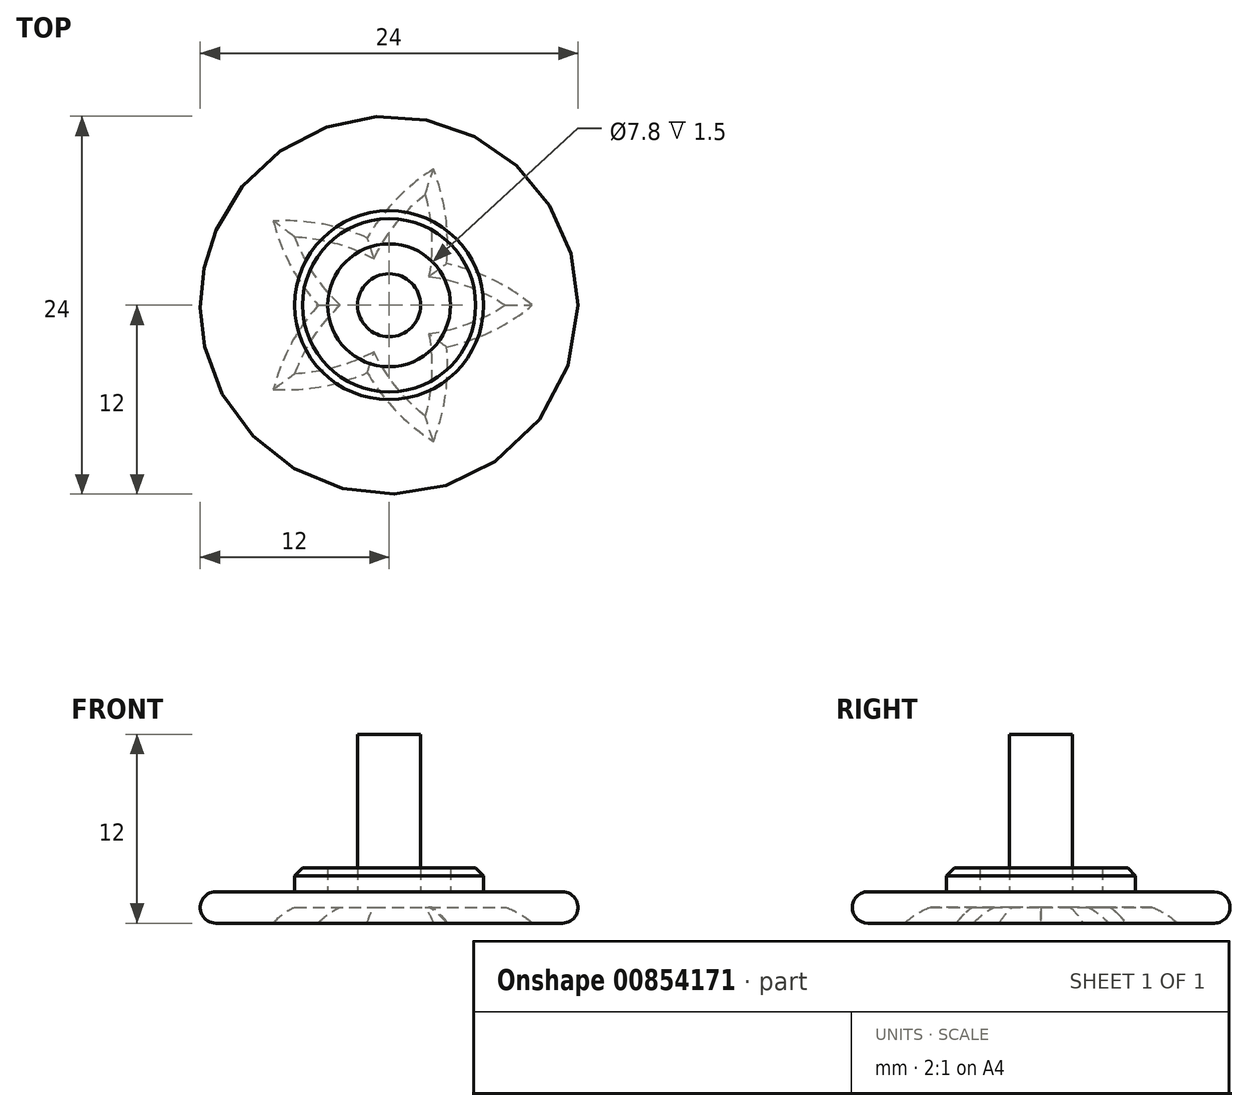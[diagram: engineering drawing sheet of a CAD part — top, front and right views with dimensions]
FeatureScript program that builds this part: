
annotation { "Feature Type Name" : "Feature", "Feature Type Description" : "" }
export const myFeature = defineFeature(function(context is Context, id is Id, definition is map)
    precondition{}
    {
        {
            var Q0;
            Q0=qCreatedBy(makeId("Top.planeOp"),FACE);
            var sketch = newSketch(context, id + "F0", { "sketchPlane" : qUnion([Q0])});
            skCircle(sketch, "E0", {"center": v(0, 0) * mm, "radius": 3.9 * mm});
            skCircle(sketch, "E1", {"center": v(0, 0) * mm, "radius": 2 * mm});
            skCircle(sketch, "E2", {"center": v(0, 0) * mm, "radius": 12 * mm});
            skCircle(sketch, "E3", {"center": v(0, 0) * mm, "radius": 6 * mm});
            skCircle(sketch, "E4.cCircle", {"center": v(0, 0) * mm, "radius": 2.5 * mm, "construction": true});
            skLineSegment(sketch, "E4.0", {"start": v(-2.5, -1.82) * mm, "end": v(-2.5, 1.82) * mm});
            skLineSegment(sketch, "E4.1", {"start": v(-2.5, 1.82) * mm, "end": v(0.95, 2.94) * mm});
            skLineSegment(sketch, "E4.2", {"start": v(0.95, 2.94) * mm, "end": v(3.1, 0) * mm});
            skLineSegment(sketch, "E4.3", {"start": v(3.1, 0) * mm, "end": v(0.95, -2.94) * mm});
            skLineSegment(sketch, "E4.4", {"start": v(0.95, -2.94) * mm, "end": v(-2.5, -1.82) * mm});
            skPoint(sketch, "E4.0.midPoint", {"position": v(-2.5, 0) * mm});
            skLineSegment(sketch, "E5", {"start": v(-2.5, 0) * mm, "end": v(-4.5, 0) * mm});
            skLineSegment(sketch, "E6", {"start": v(-0.77, -2.38) * mm, "end": v(-1.4, -4.28) * mm});
            skLineSegment(sketch, "E7", {"start": v(2.02, -1.47) * mm, "end": v(3.64, -2.65) * mm});
            skLineSegment(sketch, "E8", {"start": v(2.02, 1.47) * mm, "end": v(3.64, 2.65) * mm});
            skLineSegment(sketch, "E9", {"start": v(-0.77, 2.38) * mm, "end": v(-1.4, 4.28) * mm});
            skLineSegment(sketch, "E10", {"start": v(3.1, 0) * mm, "end": v(9.1, 0) * mm});
            skLineSegment(sketch, "E11", {"start": v(0.95, -2.94) * mm, "end": v(2.8, -8.65) * mm});
            skLineSegment(sketch, "E12", {"start": v(-2.5, -1.82) * mm, "end": v(-7.35, -5.34) * mm});
            skLineSegment(sketch, "E13", {"start": v(-2.5, 1.82) * mm, "end": v(-7.35, 5.34) * mm});
            skLineSegment(sketch, "E14", {"start": v(0.95, 2.94) * mm, "end": v(2.8, 8.65) * mm});
            skArc(sketch, "E15", {"start": v(0.95, 2.94) * mm, "mid": v(-3, 4.86) * mm, "end": v(-7.35, 5.34) * mm});
            skArc(sketch, "E16", {"start": v(2.8, 8.65) * mm, "mid": v(-0.44, 5.7) * mm, "end": v(-2.5, 1.82) * mm});
            skArc(sketch, "E17", {"start": v(3.1, 0) * mm, "mid": v(3.7, 4.35) * mm, "end": v(2.8, 8.65) * mm});
            skArc(sketch, "E18", {"start": v(9.1, 0) * mm, "mid": v(5.28, 2.17) * mm, "end": v(0.95, 2.94) * mm});
            skArc(sketch, "E19", {"start": v(0.95, -2.94) * mm, "mid": v(5.28, -2.17) * mm, "end": v(9.1, 0) * mm});
            skArc(sketch, "E20", {"start": v(2.8, -8.65) * mm, "mid": v(3.7, -4.35) * mm, "end": v(3.1, 0) * mm});
            skArc(sketch, "E21", {"start": v(-2.5, -1.82) * mm, "mid": v(-0.44, -5.7) * mm, "end": v(2.8, -8.65) * mm});
            skArc(sketch, "E22", {"start": v(-7.35, -5.34) * mm, "mid": v(-3, -4.86) * mm, "end": v(0.95, -2.94) * mm});
            skArc(sketch, "E23", {"start": v(-2.5, 1.82) * mm, "mid": v(-5.55, -1.34) * mm, "end": v(-7.35, -5.34) * mm});
            skArc(sketch, "E24", {"start": v(-7.35, 5.34) * mm, "mid": v(-5.55, 1.34) * mm, "end": v(-2.5, -1.82) * mm});
            skSolve(sketch);
        }
        {
            var Q0;
            Q0=makeQuery(id+"F0.imprint","IMPRINT",FACE,{"disambiguationData":[TD([[makeQuery(id+"F0.imprint","IMPRINT",EDGE,{"derivedFrom":sQuery(id+"F0.wireOp",EDGE,"E2")}),1.0]])]});
            extrude(context, id + "F1", {"entities" : qUnion([Q0]), "depth" : 2 * mm, "offsetDistance" : 25 * mm});
        }
        {
            var Q0;
            {var subQ0=sQuery(id+"F0.wireOp",EDGE,"E15");var subQ1=sQuery(id+"F0.wireOp",EDGE,"E3");var subQ2=makeQuery(id+"F0.imprint","INTERSECT",VERTEX,{"derivedFrom":[subQ1,subQ0]});Q0=makeQuery(id+"F0.imprint","IMPRINT",FACE,{"disambiguationData":[TD([[makeQuery(id+"F0.imprint","IMPRINT",EDGE,{"disambiguationData":[TD([[subQ2,-1.0]])],"derivedFrom":subQ1}),-1.0]])]});}
            var Q1;
            {var subQ0=sQuery(id+"F0.wireOp",EDGE,"E13");var subQ1=sQuery(id+"F0.wireOp",EDGE,"E3");var subQ2=makeQuery(id+"F0.imprint","INTERSECT",VERTEX,{"derivedFrom":[subQ1,subQ0]});Q1=makeQuery(id+"F0.imprint","IMPRINT",FACE,{"disambiguationData":[TD([[makeQuery(id+"F0.imprint","IMPRINT",EDGE,{"disambiguationData":[TD([[subQ2,-1.0]])],"derivedFrom":subQ1}),-1.0]])]});}
            var Q2;
            {var subQ3=sQuery(id+"F0.wireOp",EDGE,"E0");var subQ5=sQuery(id+"F0.wireOp",EDGE,"E13");var subQ9=makeQuery(id+"F0.imprint","INTERSECT",VERTEX,{"derivedFrom":[subQ3,subQ5]});Q2=makeQuery(id+"F0.imprint","IMPRINT",FACE,{"disambiguationData":[TD([[makeQuery(id+"F0.imprint","IMPRINT",EDGE,{"disambiguationData":[TD([[subQ9,-1.0]])],"derivedFrom":subQ3}),-1.0]])]});}
            var Q3;
            {var subQ0=sQuery(id+"F0.wireOp",EDGE,"E16");var subQ6=sQuery(id+"F0.wireOp",EDGE,"E0");var subQ9=makeQuery(id+"F0.imprint","INTERSECT",VERTEX,{"derivedFrom":[subQ6,subQ0]});Q3=makeQuery(id+"F0.imprint","IMPRINT",FACE,{"disambiguationData":[TD([[makeQuery(id+"F0.imprint","IMPRINT",EDGE,{"disambiguationData":[TD([[subQ9,-1.0]])],"derivedFrom":subQ6}),-1.0]])]});}
            var Q4;
            {var subQ3=sQuery(id+"F0.wireOp",EDGE,"E0");var subQ5=sQuery(id+"F0.wireOp",EDGE,"E14");var subQ6=makeQuery(id+"F0.imprint","INTERSECT",VERTEX,{"derivedFrom":[subQ3,subQ5]});Q4=makeQuery(id+"F0.imprint","IMPRINT",FACE,{"disambiguationData":[TD([[makeQuery(id+"F0.imprint","IMPRINT",EDGE,{"disambiguationData":[TD([[subQ6,-1.0]])],"derivedFrom":subQ3}),-1.0]])]});}
            var Q5;
            {var subQ0=sQuery(id+"F0.wireOp",EDGE,"E14");var subQ1=sQuery(id+"F0.wireOp",EDGE,"E3");var subQ2=makeQuery(id+"F0.imprint","INTERSECT",VERTEX,{"derivedFrom":[subQ1,subQ0]});Q5=makeQuery(id+"F0.imprint","IMPRINT",FACE,{"disambiguationData":[TD([[makeQuery(id+"F0.imprint","IMPRINT",EDGE,{"disambiguationData":[TD([[subQ2,-1.0]])],"derivedFrom":subQ1}),-1.0]])]});}
            var Q6;
            {var subQ0=sQuery(id+"F0.wireOp",EDGE,"E17");var subQ1=sQuery(id+"F0.wireOp",EDGE,"E3");var subQ2=makeQuery(id+"F0.imprint","INTERSECT",VERTEX,{"derivedFrom":[subQ1,subQ0]});Q6=makeQuery(id+"F0.imprint","IMPRINT",FACE,{"disambiguationData":[TD([[makeQuery(id+"F0.imprint","IMPRINT",EDGE,{"disambiguationData":[TD([[subQ2,-1.0]])],"derivedFrom":subQ1}),-1.0]])]});}
            var Q7;
            {var subQ0=sQuery(id+"F0.wireOp",EDGE,"E18");var subQ6=sQuery(id+"F0.wireOp",EDGE,"E0");var subQ9=makeQuery(id+"F0.imprint","INTERSECT",VERTEX,{"derivedFrom":[subQ6,subQ0]});Q7=makeQuery(id+"F0.imprint","IMPRINT",FACE,{"disambiguationData":[TD([[makeQuery(id+"F0.imprint","IMPRINT",EDGE,{"disambiguationData":[TD([[subQ9,-1.0]])],"derivedFrom":subQ6}),-1.0]])]});}
            var Q8;
            {var subQ0=sQuery(id+"F0.wireOp",EDGE,"E15");var subQ1=sQuery(id+"F0.wireOp",EDGE,"E0");var subQ2=makeQuery(id+"F0.imprint","INTERSECT",VERTEX,{"derivedFrom":[subQ1,subQ0]});Q8=makeQuery(id+"F0.imprint","IMPRINT",FACE,{"disambiguationData":[TD([[makeQuery(id+"F0.imprint","IMPRINT",EDGE,{"disambiguationData":[TD([[subQ2,-1.0]])],"derivedFrom":subQ1}),-1.0]])]});}
            var Q9;
            {var subQ0=sQuery(id+"F0.wireOp",EDGE,"E9");var subQ1=sQuery(id+"F0.wireOp",EDGE,"E0");var subQ2=makeQuery(id+"F0.imprint","INTERSECT",VERTEX,{"derivedFrom":[subQ1,subQ0]});Q9=makeQuery(id+"F0.imprint","IMPRINT",FACE,{"disambiguationData":[TD([[makeQuery(id+"F0.imprint","IMPRINT",EDGE,{"disambiguationData":[TD([[subQ2,-1.0]])],"derivedFrom":subQ1}),-1.0]])]});}
            var Q10;
            {var subQ0=sQuery(id+"F0.wireOp",EDGE,"E15");var subQ1=sQuery(id+"F0.wireOp",EDGE,"E0");var subQ2=makeQuery(id+"F0.imprint","INTERSECT",VERTEX,{"derivedFrom":[subQ1,subQ0]});Q10=makeQuery(id+"F0.imprint","IMPRINT",FACE,{"disambiguationData":[TD([[makeQuery(id+"F0.imprint","IMPRINT",EDGE,{"disambiguationData":[TD([[subQ2,-1.0]])],"derivedFrom":subQ1}),1.0]])]});}
            var Q11;
            {var subQ0=sQuery(id+"F0.wireOp",EDGE,"E9");var subQ1=sQuery(id+"F0.wireOp",EDGE,"E0");var subQ2=makeQuery(id+"F0.imprint","INTERSECT",VERTEX,{"derivedFrom":[subQ1,subQ0]});Q11=makeQuery(id+"F0.imprint","IMPRINT",FACE,{"disambiguationData":[TD([[makeQuery(id+"F0.imprint","IMPRINT",EDGE,{"disambiguationData":[TD([[subQ2,-1.0]])],"derivedFrom":subQ1}),1.0]])]});}
            var Q12;
            {var subQ0=sQuery(id+"F0.wireOp",EDGE,"E21");var subQ1=sQuery(id+"F0.wireOp",EDGE,"E3");var subQ2=makeQuery(id+"F0.imprint","INTERSECT",VERTEX,{"derivedFrom":[subQ1,subQ0]});Q12=makeQuery(id+"F0.imprint","IMPRINT",FACE,{"disambiguationData":[TD([[makeQuery(id+"F0.imprint","IMPRINT",EDGE,{"disambiguationData":[TD([[subQ2,-1.0]])],"derivedFrom":subQ1}),-1.0]])]});}
            var Q13;
            {var subQ0=sQuery(id+"F0.wireOp",EDGE,"E11");var subQ1=sQuery(id+"F0.wireOp",EDGE,"E3");var subQ2=makeQuery(id+"F0.imprint","INTERSECT",VERTEX,{"derivedFrom":[subQ1,subQ0]});Q13=makeQuery(id+"F0.imprint","IMPRINT",FACE,{"disambiguationData":[TD([[makeQuery(id+"F0.imprint","IMPRINT",EDGE,{"disambiguationData":[TD([[subQ2,-1.0]])],"derivedFrom":subQ1}),-1.0]])]});}
            var Q14;
            {var subQ0=sQuery(id+"F0.wireOp",EDGE,"E10");var subQ1=sQuery(id+"F0.wireOp",EDGE,"E3");var subQ2=makeQuery(id+"F0.imprint","INTERSECT",VERTEX,{"derivedFrom":[subQ1,subQ0]});Q14=makeQuery(id+"F0.imprint","IMPRINT",FACE,{"disambiguationData":[TD([[makeQuery(id+"F0.imprint","IMPRINT",EDGE,{"disambiguationData":[TD([[subQ2,1.0]])],"derivedFrom":subQ1}),-1.0]])]});}
            var Q15;
            {var subQ0=sQuery(id+"F0.wireOp",EDGE,"E18");var subQ1=sQuery(id+"F0.wireOp",EDGE,"E3");var subQ2=makeQuery(id+"F0.imprint","INTERSECT",VERTEX,{"derivedFrom":[subQ1,subQ0]});Q15=makeQuery(id+"F0.imprint","IMPRINT",FACE,{"disambiguationData":[TD([[makeQuery(id+"F0.imprint","IMPRINT",EDGE,{"disambiguationData":[TD([[subQ2,1.0]])],"derivedFrom":subQ1}),-1.0]])]});}
            var Q16;
            {var subQ0=sQuery(id+"F0.wireOp",EDGE,"E12");var subQ1=sQuery(id+"F0.wireOp",EDGE,"E3");var subQ2=makeQuery(id+"F0.imprint","INTERSECT",VERTEX,{"derivedFrom":[subQ1,subQ0]});Q16=makeQuery(id+"F0.imprint","IMPRINT",FACE,{"disambiguationData":[TD([[makeQuery(id+"F0.imprint","IMPRINT",EDGE,{"disambiguationData":[TD([[subQ2,-1.0]])],"derivedFrom":subQ1}),-1.0]])]});}
            var Q17;
            {var subQ0=sQuery(id+"F0.wireOp",EDGE,"E23");var subQ1=sQuery(id+"F0.wireOp",EDGE,"E3");var subQ2=makeQuery(id+"F0.imprint","INTERSECT",VERTEX,{"derivedFrom":[subQ1,subQ0]});Q17=makeQuery(id+"F0.imprint","IMPRINT",FACE,{"disambiguationData":[TD([[makeQuery(id+"F0.imprint","IMPRINT",EDGE,{"disambiguationData":[TD([[subQ2,-1.0]])],"derivedFrom":subQ1}),-1.0]])]});}
            var Q18;
            {var subQ1=sQuery(id+"F0.wireOp",EDGE,"E0");var subQ7=sQuery(id+"F0.wireOp",EDGE,"E24");var subQ9=makeQuery(id+"F0.imprint","INTERSECT",VERTEX,{"derivedFrom":[subQ1,subQ7]});Q18=makeQuery(id+"F0.imprint","IMPRINT",FACE,{"disambiguationData":[TD([[makeQuery(id+"F0.imprint","IMPRINT",EDGE,{"disambiguationData":[TD([[subQ9,-1.0]])],"derivedFrom":subQ1}),-1.0]])]});}
            var Q19;
            {var subQ0=sQuery(id+"F0.wireOp",EDGE,"E12");var subQ1=sQuery(id+"F0.wireOp",EDGE,"E0");var subQ2=makeQuery(id+"F0.imprint","INTERSECT",VERTEX,{"derivedFrom":[subQ1,subQ0]});Q19=makeQuery(id+"F0.imprint","IMPRINT",FACE,{"disambiguationData":[TD([[makeQuery(id+"F0.imprint","IMPRINT",EDGE,{"disambiguationData":[TD([[subQ2,-1.0]])],"derivedFrom":subQ1}),-1.0]])]});}
            var Q20;
            {var subQ1=sQuery(id+"F0.wireOp",EDGE,"E0");var subQ5=sQuery(id+"F0.wireOp",EDGE,"E22");var subQ9=makeQuery(id+"F0.imprint","INTERSECT",VERTEX,{"derivedFrom":[subQ1,subQ5]});Q20=makeQuery(id+"F0.imprint","IMPRINT",FACE,{"disambiguationData":[TD([[makeQuery(id+"F0.imprint","IMPRINT",EDGE,{"disambiguationData":[TD([[subQ9,-1.0]])],"derivedFrom":subQ1}),-1.0]])]});}
            var Q21;
            {var subQ3=sQuery(id+"F0.wireOp",EDGE,"E0");var subQ5=sQuery(id+"F0.wireOp",EDGE,"E11");var subQ9=makeQuery(id+"F0.imprint","INTERSECT",VERTEX,{"derivedFrom":[subQ3,subQ5]});Q21=makeQuery(id+"F0.imprint","IMPRINT",FACE,{"disambiguationData":[TD([[makeQuery(id+"F0.imprint","IMPRINT",EDGE,{"disambiguationData":[TD([[subQ9,-1.0]])],"derivedFrom":subQ3}),-1.0]])]});}
            var Q22;
            {var subQ5=sQuery(id+"F0.wireOp",EDGE,"E10");var subQ6=sQuery(id+"F0.wireOp",EDGE,"E0");var subQ7=makeQuery(id+"F0.imprint","INTERSECT",VERTEX,{"derivedFrom":[subQ6,subQ5]});Q22=makeQuery(id+"F0.imprint","IMPRINT",FACE,{"disambiguationData":[TD([[makeQuery(id+"F0.imprint","IMPRINT",EDGE,{"disambiguationData":[TD([[subQ7,1.0]])],"derivedFrom":subQ6}),-1.0]])]});}
            var Q23;
            {var subQ1=sQuery(id+"F0.wireOp",EDGE,"E17");var subQ3=sQuery(id+"F0.wireOp",EDGE,"E0");var subQ4=makeQuery(id+"F0.imprint","INTERSECT",VERTEX,{"derivedFrom":[subQ3,subQ1]});Q23=makeQuery(id+"F0.imprint","IMPRINT",FACE,{"disambiguationData":[TD([[makeQuery(id+"F0.imprint","IMPRINT",EDGE,{"disambiguationData":[TD([[subQ4,1.0]])],"derivedFrom":subQ3}),-1.0]])]});}
            var Q24;
            {var subQ0=sQuery(id+"F0.wireOp",EDGE,"E8");var subQ1=sQuery(id+"F0.wireOp",EDGE,"E0");var subQ2=makeQuery(id+"F0.imprint","INTERSECT",VERTEX,{"derivedFrom":[subQ1,subQ0]});Q24=makeQuery(id+"F0.imprint","IMPRINT",FACE,{"disambiguationData":[TD([[makeQuery(id+"F0.imprint","IMPRINT",EDGE,{"disambiguationData":[TD([[subQ2,-1.0]])],"derivedFrom":subQ1}),1.0]])]});}
            var Q25;
            {var subQ0=sQuery(id+"F0.wireOp",EDGE,"E17");var subQ1=sQuery(id+"F0.wireOp",EDGE,"E0");var subQ2=makeQuery(id+"F0.imprint","INTERSECT",VERTEX,{"derivedFrom":[subQ1,subQ0]});Q25=makeQuery(id+"F0.imprint","IMPRINT",FACE,{"disambiguationData":[TD([[makeQuery(id+"F0.imprint","IMPRINT",EDGE,{"disambiguationData":[TD([[subQ2,-1.0]])],"derivedFrom":subQ1}),1.0]])]});}
            var Q26;
            {var subQ0=sQuery(id+"F0.wireOp",EDGE,"E8");var subQ1=sQuery(id+"F0.wireOp",EDGE,"E0");var subQ2=makeQuery(id+"F0.imprint","INTERSECT",VERTEX,{"derivedFrom":[subQ1,subQ0]});Q26=makeQuery(id+"F0.imprint","IMPRINT",FACE,{"disambiguationData":[TD([[makeQuery(id+"F0.imprint","IMPRINT",EDGE,{"disambiguationData":[TD([[subQ2,-1.0]])],"derivedFrom":subQ1}),-1.0]])]});}
            var Q27;
            {var subQ0=sQuery(id+"F0.wireOp",EDGE,"E17");var subQ1=sQuery(id+"F0.wireOp",EDGE,"E0");var subQ2=makeQuery(id+"F0.imprint","INTERSECT",VERTEX,{"derivedFrom":[subQ1,subQ0]});Q27=makeQuery(id+"F0.imprint","IMPRINT",FACE,{"disambiguationData":[TD([[makeQuery(id+"F0.imprint","IMPRINT",EDGE,{"disambiguationData":[TD([[subQ2,-1.0]])],"derivedFrom":subQ1}),-1.0]])]});}
            var Q28;
            {var subQ0=sQuery(id+"F0.wireOp",EDGE,"E23");var subQ1=sQuery(id+"F0.wireOp",EDGE,"E0");var subQ2=makeQuery(id+"F0.imprint","INTERSECT",VERTEX,{"derivedFrom":[subQ1,subQ0]});Q28=makeQuery(id+"F0.imprint","IMPRINT",FACE,{"disambiguationData":[TD([[makeQuery(id+"F0.imprint","IMPRINT",EDGE,{"disambiguationData":[TD([[subQ2,-1.0]])],"derivedFrom":subQ1}),-1.0]])]});}
            var Q29;
            {var subQ0=sQuery(id+"F0.wireOp",EDGE,"E5");var subQ1=sQuery(id+"F0.wireOp",EDGE,"E0");var subQ2=makeQuery(id+"F0.imprint","INTERSECT",VERTEX,{"derivedFrom":[subQ1,subQ0]});Q29=makeQuery(id+"F0.imprint","IMPRINT",FACE,{"disambiguationData":[TD([[makeQuery(id+"F0.imprint","IMPRINT",EDGE,{"disambiguationData":[TD([[subQ2,-1.0]])],"derivedFrom":subQ1}),-1.0]])]});}
            var Q30;
            {var subQ0=sQuery(id+"F0.wireOp",EDGE,"E21");var subQ1=sQuery(id+"F0.wireOp",EDGE,"E0");var subQ2=makeQuery(id+"F0.imprint","INTERSECT",VERTEX,{"derivedFrom":[subQ1,subQ0]});Q30=makeQuery(id+"F0.imprint","IMPRINT",FACE,{"disambiguationData":[TD([[makeQuery(id+"F0.imprint","IMPRINT",EDGE,{"disambiguationData":[TD([[subQ2,-1.0]])],"derivedFrom":subQ1}),-1.0]])]});}
            var Q31;
            {var subQ0=sQuery(id+"F0.wireOp",EDGE,"E6");var subQ1=sQuery(id+"F0.wireOp",EDGE,"E0");var subQ2=makeQuery(id+"F0.imprint","INTERSECT",VERTEX,{"derivedFrom":[subQ1,subQ0]});Q31=makeQuery(id+"F0.imprint","IMPRINT",FACE,{"disambiguationData":[TD([[makeQuery(id+"F0.imprint","IMPRINT",EDGE,{"disambiguationData":[TD([[subQ2,-1.0]])],"derivedFrom":subQ1}),-1.0]])]});}
            var Q32;
            {var subQ0=sQuery(id+"F0.wireOp",EDGE,"E19");var subQ1=sQuery(id+"F0.wireOp",EDGE,"E0");var subQ2=makeQuery(id+"F0.imprint","INTERSECT",VERTEX,{"derivedFrom":[subQ1,subQ0]});Q32=makeQuery(id+"F0.imprint","IMPRINT",FACE,{"disambiguationData":[TD([[makeQuery(id+"F0.imprint","IMPRINT",EDGE,{"disambiguationData":[TD([[subQ2,-1.0]])],"derivedFrom":subQ1}),-1.0]])]});}
            var Q33;
            {var subQ0=sQuery(id+"F0.wireOp",EDGE,"E7");var subQ1=sQuery(id+"F0.wireOp",EDGE,"E0");var subQ2=makeQuery(id+"F0.imprint","INTERSECT",VERTEX,{"derivedFrom":[subQ1,subQ0]});Q33=makeQuery(id+"F0.imprint","IMPRINT",FACE,{"disambiguationData":[TD([[makeQuery(id+"F0.imprint","IMPRINT",EDGE,{"disambiguationData":[TD([[subQ2,-1.0]])],"derivedFrom":subQ1}),-1.0]])]});}
            var Q34;
            {var subQ0=sQuery(id+"F0.wireOp",EDGE,"E10");var subQ1=sQuery(id+"F0.wireOp",EDGE,"E0");var subQ2=makeQuery(id+"F0.imprint","INTERSECT",VERTEX,{"derivedFrom":[subQ1,subQ0]});Q34=makeQuery(id+"F0.imprint","IMPRINT",FACE,{"disambiguationData":[TD([[makeQuery(id+"F0.imprint","IMPRINT",EDGE,{"disambiguationData":[TD([[subQ2,1.0]])],"derivedFrom":subQ1}),1.0]])]});}
            var Q35;
            {var subQ0=sQuery(id+"F0.wireOp",EDGE,"E17");var subQ1=sQuery(id+"F0.wireOp",EDGE,"E0");var subQ2=makeQuery(id+"F0.imprint","INTERSECT",VERTEX,{"derivedFrom":[subQ1,subQ0]});Q35=makeQuery(id+"F0.imprint","IMPRINT",FACE,{"disambiguationData":[TD([[makeQuery(id+"F0.imprint","IMPRINT",EDGE,{"disambiguationData":[TD([[subQ2,1.0]])],"derivedFrom":subQ1}),1.0]])]});}
            var Q36;
            {var subQ0=sQuery(id+"F0.wireOp",EDGE,"E18");var subQ1=sQuery(id+"F0.wireOp",EDGE,"E0");var subQ2=makeQuery(id+"F0.imprint","INTERSECT",VERTEX,{"derivedFrom":[subQ1,subQ0]});Q36=makeQuery(id+"F0.imprint","IMPRINT",FACE,{"disambiguationData":[TD([[makeQuery(id+"F0.imprint","IMPRINT",EDGE,{"disambiguationData":[TD([[subQ2,-1.0]])],"derivedFrom":subQ1}),1.0]])]});}
            var Q37;
            {var subQ0=sQuery(id+"F0.wireOp",EDGE,"E14");var subQ1=sQuery(id+"F0.wireOp",EDGE,"E0");var subQ2=makeQuery(id+"F0.imprint","INTERSECT",VERTEX,{"derivedFrom":[subQ1,subQ0]});Q37=makeQuery(id+"F0.imprint","IMPRINT",FACE,{"disambiguationData":[TD([[makeQuery(id+"F0.imprint","IMPRINT",EDGE,{"disambiguationData":[TD([[subQ2,-1.0]])],"derivedFrom":subQ1}),1.0]])]});}
            var Q38;
            {var subQ0=sQuery(id+"F0.wireOp",EDGE,"E16");var subQ1=sQuery(id+"F0.wireOp",EDGE,"E0");var subQ2=makeQuery(id+"F0.imprint","INTERSECT",VERTEX,{"derivedFrom":[subQ1,subQ0]});Q38=makeQuery(id+"F0.imprint","IMPRINT",FACE,{"disambiguationData":[TD([[makeQuery(id+"F0.imprint","IMPRINT",EDGE,{"disambiguationData":[TD([[subQ2,-1.0]])],"derivedFrom":subQ1}),1.0]])]});}
            var Q39;
            {var subQ0=sQuery(id+"F0.wireOp",EDGE,"E13");var subQ1=sQuery(id+"F0.wireOp",EDGE,"E0");var subQ2=makeQuery(id+"F0.imprint","INTERSECT",VERTEX,{"derivedFrom":[subQ1,subQ0]});Q39=makeQuery(id+"F0.imprint","IMPRINT",FACE,{"disambiguationData":[TD([[makeQuery(id+"F0.imprint","IMPRINT",EDGE,{"disambiguationData":[TD([[subQ2,-1.0]])],"derivedFrom":subQ1}),1.0]])]});}
            var Q40;
            {var subQ0=sQuery(id+"F0.wireOp",EDGE,"E24");var subQ1=sQuery(id+"F0.wireOp",EDGE,"E0");var subQ2=makeQuery(id+"F0.imprint","INTERSECT",VERTEX,{"derivedFrom":[subQ1,subQ0]});Q40=makeQuery(id+"F0.imprint","IMPRINT",FACE,{"disambiguationData":[TD([[makeQuery(id+"F0.imprint","IMPRINT",EDGE,{"disambiguationData":[TD([[subQ2,-1.0]])],"derivedFrom":subQ1}),1.0]])]});}
            var Q41;
            {var subQ0=sQuery(id+"F0.wireOp",EDGE,"E12");var subQ1=sQuery(id+"F0.wireOp",EDGE,"E0");var subQ2=makeQuery(id+"F0.imprint","INTERSECT",VERTEX,{"derivedFrom":[subQ1,subQ0]});Q41=makeQuery(id+"F0.imprint","IMPRINT",FACE,{"disambiguationData":[TD([[makeQuery(id+"F0.imprint","IMPRINT",EDGE,{"disambiguationData":[TD([[subQ2,-1.0]])],"derivedFrom":subQ1}),1.0]])]});}
            var Q42;
            {var subQ0=sQuery(id+"F0.wireOp",EDGE,"E22");var subQ1=sQuery(id+"F0.wireOp",EDGE,"E0");var subQ2=makeQuery(id+"F0.imprint","INTERSECT",VERTEX,{"derivedFrom":[subQ1,subQ0]});Q42=makeQuery(id+"F0.imprint","IMPRINT",FACE,{"disambiguationData":[TD([[makeQuery(id+"F0.imprint","IMPRINT",EDGE,{"disambiguationData":[TD([[subQ2,-1.0]])],"derivedFrom":subQ1}),1.0]])]});}
            var Q43;
            {var subQ0=sQuery(id+"F0.wireOp",EDGE,"E11");var subQ1=sQuery(id+"F0.wireOp",EDGE,"E0");var subQ2=makeQuery(id+"F0.imprint","INTERSECT",VERTEX,{"derivedFrom":[subQ1,subQ0]});Q43=makeQuery(id+"F0.imprint","IMPRINT",FACE,{"disambiguationData":[TD([[makeQuery(id+"F0.imprint","IMPRINT",EDGE,{"disambiguationData":[TD([[subQ2,-1.0]])],"derivedFrom":subQ1}),1.0]])]});}
            var Q44;
            {var subQ0=sQuery(id+"F0.wireOp",EDGE,"E19");var subQ1=sQuery(id+"F0.wireOp",EDGE,"E0");var subQ2=makeQuery(id+"F0.imprint","INTERSECT",VERTEX,{"derivedFrom":[subQ1,subQ0]});Q44=makeQuery(id+"F0.imprint","IMPRINT",FACE,{"disambiguationData":[TD([[makeQuery(id+"F0.imprint","IMPRINT",EDGE,{"disambiguationData":[TD([[subQ2,-1.0]])],"derivedFrom":subQ1}),1.0]])]});}
            var Q45;
            {var subQ0=sQuery(id+"F0.wireOp",EDGE,"E7");var subQ1=sQuery(id+"F0.wireOp",EDGE,"E0");var subQ2=makeQuery(id+"F0.imprint","INTERSECT",VERTEX,{"derivedFrom":[subQ1,subQ0]});Q45=makeQuery(id+"F0.imprint","IMPRINT",FACE,{"disambiguationData":[TD([[makeQuery(id+"F0.imprint","IMPRINT",EDGE,{"disambiguationData":[TD([[subQ2,-1.0]])],"derivedFrom":subQ1}),1.0]])]});}
            var Q46;
            {var subQ0=sQuery(id+"F0.wireOp",EDGE,"E6");var subQ1=sQuery(id+"F0.wireOp",EDGE,"E0");var subQ2=makeQuery(id+"F0.imprint","INTERSECT",VERTEX,{"derivedFrom":[subQ1,subQ0]});Q46=makeQuery(id+"F0.imprint","IMPRINT",FACE,{"disambiguationData":[TD([[makeQuery(id+"F0.imprint","IMPRINT",EDGE,{"disambiguationData":[TD([[subQ2,-1.0]])],"derivedFrom":subQ1}),1.0]])]});}
            var Q47;
            {var subQ0=sQuery(id+"F0.wireOp",EDGE,"E21");var subQ1=sQuery(id+"F0.wireOp",EDGE,"E0");var subQ2=makeQuery(id+"F0.imprint","INTERSECT",VERTEX,{"derivedFrom":[subQ1,subQ0]});Q47=makeQuery(id+"F0.imprint","IMPRINT",FACE,{"disambiguationData":[TD([[makeQuery(id+"F0.imprint","IMPRINT",EDGE,{"disambiguationData":[TD([[subQ2,-1.0]])],"derivedFrom":subQ1}),1.0]])]});}
            var Q48;
            {var subQ0=sQuery(id+"F0.wireOp",EDGE,"E5");var subQ1=sQuery(id+"F0.wireOp",EDGE,"E0");var subQ2=makeQuery(id+"F0.imprint","INTERSECT",VERTEX,{"derivedFrom":[subQ1,subQ0]});Q48=makeQuery(id+"F0.imprint","IMPRINT",FACE,{"disambiguationData":[TD([[makeQuery(id+"F0.imprint","IMPRINT",EDGE,{"disambiguationData":[TD([[subQ2,-1.0]])],"derivedFrom":subQ1}),1.0]])]});}
            var Q49;
            {var subQ0=sQuery(id+"F0.wireOp",EDGE,"E23");var subQ1=sQuery(id+"F0.wireOp",EDGE,"E0");var subQ2=makeQuery(id+"F0.imprint","INTERSECT",VERTEX,{"derivedFrom":[subQ1,subQ0]});Q49=makeQuery(id+"F0.imprint","IMPRINT",FACE,{"disambiguationData":[TD([[makeQuery(id+"F0.imprint","IMPRINT",EDGE,{"disambiguationData":[TD([[subQ2,-1.0]])],"derivedFrom":subQ1}),1.0]])]});}
            var Q50;
            Q50=makeQuery(id+"F0.imprint","IMPRINT",FACE,{"disambiguationData":[TD([[makeQuery(id+"F0.imprint","IMPRINT",EDGE,{"derivedFrom":sQuery(id+"F0.wireOp",EDGE,"E1")}),-1.0]])]});
            var Q51;
            Q51=makeQuery(id+"F0.imprint","IMPRINT",FACE,{"disambiguationData":[TD([[makeQuery(id+"F0.imprint","IMPRINT",EDGE,{"derivedFrom":sQuery(id+"F0.wireOp",EDGE,"E1")}),1.0]])]});
            extrude(context, id + "F2", {"entities" : qUnion([Q0, Q1, Q2, Q3, Q4, Q5, Q6, Q7, Q8, Q9, Q10, Q11, Q12, Q13, Q14, Q15, Q16, Q17, Q18, Q19, Q20, Q21, Q22, Q23, Q24, Q25, Q26, Q27, Q28, Q29, Q30, Q31, Q32, Q33, Q34, Q35, Q36, Q37, Q38, Q39, Q40, Q41, Q42, Q43, Q44, Q45, Q46, Q47, Q48, Q49, Q50, Q51]), "operationType" : NewBodyOperationType.ADD, "depth" : 2 * mm, "offsetDistance" : 25 * mm, "hasSecondDirection" : true, "secondDirectionOppositeDirection" : false, "secondDirectionDepth" : 1 * mm});
        }
        {
            var Q0;
            {var subQ0=sQuery(id+"F0.wireOp",EDGE,"E24");var subQ1=sQuery(id+"F0.wireOp",EDGE,"E3");var subQ2=makeQuery(id+"F0.imprint","INTERSECT",VERTEX,{"derivedFrom":[subQ1,subQ0]});Q0=makeQuery(id+"F0.imprint","IMPRINT",FACE,{"disambiguationData":[TD([[makeQuery(id+"F0.imprint","IMPRINT",EDGE,{"disambiguationData":[TD([[subQ2,-1.0]])],"derivedFrom":subQ1}),1.0]])]});}
            var Q1;
            {var subQ0=sQuery(id+"F0.wireOp",EDGE,"E16");var subQ1=sQuery(id+"F0.wireOp",EDGE,"E3");var subQ2=makeQuery(id+"F0.imprint","INTERSECT",VERTEX,{"derivedFrom":[subQ1,subQ0]});Q1=makeQuery(id+"F0.imprint","IMPRINT",FACE,{"disambiguationData":[TD([[makeQuery(id+"F0.imprint","IMPRINT",EDGE,{"disambiguationData":[TD([[subQ2,-1.0]])],"derivedFrom":subQ1}),1.0]])]});}
            var Q2;
            {var subQ0=sQuery(id+"F0.wireOp",EDGE,"E18");var subQ1=sQuery(id+"F0.wireOp",EDGE,"E3");var subQ2=makeQuery(id+"F0.imprint","INTERSECT",VERTEX,{"derivedFrom":[subQ1,subQ0]});Q2=makeQuery(id+"F0.imprint","IMPRINT",FACE,{"disambiguationData":[TD([[makeQuery(id+"F0.imprint","IMPRINT",EDGE,{"disambiguationData":[TD([[subQ2,-1.0]])],"derivedFrom":subQ1}),1.0]])]});}
            var Q3;
            {var subQ0=sQuery(id+"F0.wireOp",EDGE,"E20");var subQ1=sQuery(id+"F0.wireOp",EDGE,"E3");var subQ2=makeQuery(id+"F0.imprint","INTERSECT",VERTEX,{"derivedFrom":[subQ1,subQ0]});Q3=makeQuery(id+"F0.imprint","IMPRINT",FACE,{"disambiguationData":[TD([[makeQuery(id+"F0.imprint","IMPRINT",EDGE,{"disambiguationData":[TD([[subQ2,-1.0]])],"derivedFrom":subQ1}),1.0]])]});}
            var Q4;
            {var subQ0=sQuery(id+"F0.wireOp",EDGE,"E22");var subQ1=sQuery(id+"F0.wireOp",EDGE,"E3");var subQ2=makeQuery(id+"F0.imprint","INTERSECT",VERTEX,{"derivedFrom":[subQ1,subQ0]});Q4=makeQuery(id+"F0.imprint","IMPRINT",FACE,{"disambiguationData":[TD([[makeQuery(id+"F0.imprint","IMPRINT",EDGE,{"disambiguationData":[TD([[subQ2,-1.0]])],"derivedFrom":subQ1}),1.0]])]});}
            extrude(context, id + "F3", {"entities" : qUnion([Q0, Q1, Q2, Q3, Q4]), "operationType" : NewBodyOperationType.ADD, "depth" : 3.5 * mm, "offsetDistance" : 25 * mm});
        }
        {
            var Q0;
            {var subQ0=sQuery(id+"F0.wireOp",EDGE,"E12");var subQ1=sQuery(id+"F0.wireOp",EDGE,"E0");var subQ2=makeQuery(id+"F0.imprint","INTERSECT",VERTEX,{"derivedFrom":[subQ1,subQ0]});Q0=makeQuery(id+"F0.imprint","IMPRINT",FACE,{"disambiguationData":[TD([[makeQuery(id+"F0.imprint","IMPRINT",EDGE,{"disambiguationData":[TD([[subQ2,-1.0]])],"derivedFrom":subQ1}),-1.0]])]});}
            var Q1;
            {var subQ1=sQuery(id+"F0.wireOp",EDGE,"E0");var subQ7=sQuery(id+"F0.wireOp",EDGE,"E24");var subQ9=makeQuery(id+"F0.imprint","INTERSECT",VERTEX,{"derivedFrom":[subQ1,subQ7]});Q1=makeQuery(id+"F0.imprint","IMPRINT",FACE,{"disambiguationData":[TD([[makeQuery(id+"F0.imprint","IMPRINT",EDGE,{"disambiguationData":[TD([[subQ9,-1.0]])],"derivedFrom":subQ1}),-1.0]])]});}
            var Q2;
            {var subQ1=sQuery(id+"F0.wireOp",EDGE,"E0");var subQ5=sQuery(id+"F0.wireOp",EDGE,"E22");var subQ9=makeQuery(id+"F0.imprint","INTERSECT",VERTEX,{"derivedFrom":[subQ1,subQ5]});Q2=makeQuery(id+"F0.imprint","IMPRINT",FACE,{"disambiguationData":[TD([[makeQuery(id+"F0.imprint","IMPRINT",EDGE,{"disambiguationData":[TD([[subQ9,-1.0]])],"derivedFrom":subQ1}),-1.0]])]});}
            var Q3;
            {var subQ3=sQuery(id+"F0.wireOp",EDGE,"E0");var subQ5=sQuery(id+"F0.wireOp",EDGE,"E11");var subQ9=makeQuery(id+"F0.imprint","INTERSECT",VERTEX,{"derivedFrom":[subQ3,subQ5]});Q3=makeQuery(id+"F0.imprint","IMPRINT",FACE,{"disambiguationData":[TD([[makeQuery(id+"F0.imprint","IMPRINT",EDGE,{"disambiguationData":[TD([[subQ9,-1.0]])],"derivedFrom":subQ3}),-1.0]])]});}
            var Q4;
            {var subQ0=sQuery(id+"F0.wireOp",EDGE,"E6");var subQ1=sQuery(id+"F0.wireOp",EDGE,"E0");var subQ2=makeQuery(id+"F0.imprint","INTERSECT",VERTEX,{"derivedFrom":[subQ1,subQ0]});Q4=makeQuery(id+"F0.imprint","IMPRINT",FACE,{"disambiguationData":[TD([[makeQuery(id+"F0.imprint","IMPRINT",EDGE,{"disambiguationData":[TD([[subQ2,-1.0]])],"derivedFrom":subQ1}),-1.0]])]});}
            var Q5;
            {var subQ0=sQuery(id+"F0.wireOp",EDGE,"E21");var subQ1=sQuery(id+"F0.wireOp",EDGE,"E0");var subQ2=makeQuery(id+"F0.imprint","INTERSECT",VERTEX,{"derivedFrom":[subQ1,subQ0]});Q5=makeQuery(id+"F0.imprint","IMPRINT",FACE,{"disambiguationData":[TD([[makeQuery(id+"F0.imprint","IMPRINT",EDGE,{"disambiguationData":[TD([[subQ2,-1.0]])],"derivedFrom":subQ1}),-1.0]])]});}
            var Q6;
            {var subQ0=sQuery(id+"F0.wireOp",EDGE,"E19");var subQ1=sQuery(id+"F0.wireOp",EDGE,"E0");var subQ2=makeQuery(id+"F0.imprint","INTERSECT",VERTEX,{"derivedFrom":[subQ1,subQ0]});Q6=makeQuery(id+"F0.imprint","IMPRINT",FACE,{"disambiguationData":[TD([[makeQuery(id+"F0.imprint","IMPRINT",EDGE,{"disambiguationData":[TD([[subQ2,-1.0]])],"derivedFrom":subQ1}),-1.0]])]});}
            var Q7;
            {var subQ0=sQuery(id+"F0.wireOp",EDGE,"E7");var subQ1=sQuery(id+"F0.wireOp",EDGE,"E0");var subQ2=makeQuery(id+"F0.imprint","INTERSECT",VERTEX,{"derivedFrom":[subQ1,subQ0]});Q7=makeQuery(id+"F0.imprint","IMPRINT",FACE,{"disambiguationData":[TD([[makeQuery(id+"F0.imprint","IMPRINT",EDGE,{"disambiguationData":[TD([[subQ2,-1.0]])],"derivedFrom":subQ1}),-1.0]])]});}
            var Q8;
            {var subQ5=sQuery(id+"F0.wireOp",EDGE,"E10");var subQ6=sQuery(id+"F0.wireOp",EDGE,"E0");var subQ7=makeQuery(id+"F0.imprint","INTERSECT",VERTEX,{"derivedFrom":[subQ6,subQ5]});Q8=makeQuery(id+"F0.imprint","IMPRINT",FACE,{"disambiguationData":[TD([[makeQuery(id+"F0.imprint","IMPRINT",EDGE,{"disambiguationData":[TD([[subQ7,1.0]])],"derivedFrom":subQ6}),-1.0]])]});}
            var Q9;
            {var subQ1=sQuery(id+"F0.wireOp",EDGE,"E17");var subQ3=sQuery(id+"F0.wireOp",EDGE,"E0");var subQ4=makeQuery(id+"F0.imprint","INTERSECT",VERTEX,{"derivedFrom":[subQ3,subQ1]});Q9=makeQuery(id+"F0.imprint","IMPRINT",FACE,{"disambiguationData":[TD([[makeQuery(id+"F0.imprint","IMPRINT",EDGE,{"disambiguationData":[TD([[subQ4,1.0]])],"derivedFrom":subQ3}),-1.0]])]});}
            var Q10;
            {var subQ0=sQuery(id+"F0.wireOp",EDGE,"E17");var subQ1=sQuery(id+"F0.wireOp",EDGE,"E0");var subQ2=makeQuery(id+"F0.imprint","INTERSECT",VERTEX,{"derivedFrom":[subQ1,subQ0]});Q10=makeQuery(id+"F0.imprint","IMPRINT",FACE,{"disambiguationData":[TD([[makeQuery(id+"F0.imprint","IMPRINT",EDGE,{"disambiguationData":[TD([[subQ2,-1.0]])],"derivedFrom":subQ1}),-1.0]])]});}
            var Q11;
            {var subQ0=sQuery(id+"F0.wireOp",EDGE,"E8");var subQ1=sQuery(id+"F0.wireOp",EDGE,"E0");var subQ2=makeQuery(id+"F0.imprint","INTERSECT",VERTEX,{"derivedFrom":[subQ1,subQ0]});Q11=makeQuery(id+"F0.imprint","IMPRINT",FACE,{"disambiguationData":[TD([[makeQuery(id+"F0.imprint","IMPRINT",EDGE,{"disambiguationData":[TD([[subQ2,-1.0]])],"derivedFrom":subQ1}),-1.0]])]});}
            var Q12;
            {var subQ0=sQuery(id+"F0.wireOp",EDGE,"E18");var subQ6=sQuery(id+"F0.wireOp",EDGE,"E0");var subQ9=makeQuery(id+"F0.imprint","INTERSECT",VERTEX,{"derivedFrom":[subQ6,subQ0]});Q12=makeQuery(id+"F0.imprint","IMPRINT",FACE,{"disambiguationData":[TD([[makeQuery(id+"F0.imprint","IMPRINT",EDGE,{"disambiguationData":[TD([[subQ9,-1.0]])],"derivedFrom":subQ6}),-1.0]])]});}
            var Q13;
            {var subQ3=sQuery(id+"F0.wireOp",EDGE,"E0");var subQ5=sQuery(id+"F0.wireOp",EDGE,"E14");var subQ6=makeQuery(id+"F0.imprint","INTERSECT",VERTEX,{"derivedFrom":[subQ3,subQ5]});Q13=makeQuery(id+"F0.imprint","IMPRINT",FACE,{"disambiguationData":[TD([[makeQuery(id+"F0.imprint","IMPRINT",EDGE,{"disambiguationData":[TD([[subQ6,-1.0]])],"derivedFrom":subQ3}),-1.0]])]});}
            var Q14;
            {var subQ0=sQuery(id+"F0.wireOp",EDGE,"E15");var subQ1=sQuery(id+"F0.wireOp",EDGE,"E0");var subQ2=makeQuery(id+"F0.imprint","INTERSECT",VERTEX,{"derivedFrom":[subQ1,subQ0]});Q14=makeQuery(id+"F0.imprint","IMPRINT",FACE,{"disambiguationData":[TD([[makeQuery(id+"F0.imprint","IMPRINT",EDGE,{"disambiguationData":[TD([[subQ2,-1.0]])],"derivedFrom":subQ1}),-1.0]])]});}
            var Q15;
            {var subQ0=sQuery(id+"F0.wireOp",EDGE,"E9");var subQ1=sQuery(id+"F0.wireOp",EDGE,"E0");var subQ2=makeQuery(id+"F0.imprint","INTERSECT",VERTEX,{"derivedFrom":[subQ1,subQ0]});Q15=makeQuery(id+"F0.imprint","IMPRINT",FACE,{"disambiguationData":[TD([[makeQuery(id+"F0.imprint","IMPRINT",EDGE,{"disambiguationData":[TD([[subQ2,-1.0]])],"derivedFrom":subQ1}),-1.0]])]});}
            var Q16;
            {var subQ0=sQuery(id+"F0.wireOp",EDGE,"E16");var subQ6=sQuery(id+"F0.wireOp",EDGE,"E0");var subQ9=makeQuery(id+"F0.imprint","INTERSECT",VERTEX,{"derivedFrom":[subQ6,subQ0]});Q16=makeQuery(id+"F0.imprint","IMPRINT",FACE,{"disambiguationData":[TD([[makeQuery(id+"F0.imprint","IMPRINT",EDGE,{"disambiguationData":[TD([[subQ9,-1.0]])],"derivedFrom":subQ6}),-1.0]])]});}
            var Q17;
            {var subQ3=sQuery(id+"F0.wireOp",EDGE,"E0");var subQ5=sQuery(id+"F0.wireOp",EDGE,"E13");var subQ9=makeQuery(id+"F0.imprint","INTERSECT",VERTEX,{"derivedFrom":[subQ3,subQ5]});Q17=makeQuery(id+"F0.imprint","IMPRINT",FACE,{"disambiguationData":[TD([[makeQuery(id+"F0.imprint","IMPRINT",EDGE,{"disambiguationData":[TD([[subQ9,-1.0]])],"derivedFrom":subQ3}),-1.0]])]});}
            var Q18;
            {var subQ0=sQuery(id+"F0.wireOp",EDGE,"E23");var subQ1=sQuery(id+"F0.wireOp",EDGE,"E0");var subQ2=makeQuery(id+"F0.imprint","INTERSECT",VERTEX,{"derivedFrom":[subQ1,subQ0]});Q18=makeQuery(id+"F0.imprint","IMPRINT",FACE,{"disambiguationData":[TD([[makeQuery(id+"F0.imprint","IMPRINT",EDGE,{"disambiguationData":[TD([[subQ2,-1.0]])],"derivedFrom":subQ1}),-1.0]])]});}
            var Q19;
            {var subQ0=sQuery(id+"F0.wireOp",EDGE,"E5");var subQ1=sQuery(id+"F0.wireOp",EDGE,"E0");var subQ2=makeQuery(id+"F0.imprint","INTERSECT",VERTEX,{"derivedFrom":[subQ1,subQ0]});Q19=makeQuery(id+"F0.imprint","IMPRINT",FACE,{"disambiguationData":[TD([[makeQuery(id+"F0.imprint","IMPRINT",EDGE,{"disambiguationData":[TD([[subQ2,-1.0]])],"derivedFrom":subQ1}),-1.0]])]});}
            extrude(context, id + "F4", {"entities" : qUnion([Q0, Q1, Q2, Q3, Q4, Q5, Q6, Q7, Q8, Q9, Q10, Q11, Q12, Q13, Q14, Q15, Q16, Q17, Q18, Q19]), "operationType" : NewBodyOperationType.ADD, "depth" : 3.5 * mm, "offsetDistance" : 25 * mm, "hasSecondDirection" : true, "secondDirectionOppositeDirection" : false, "secondDirectionDepth" : 1 * mm});
        }
        {
            var Q0;
            Q0=makeQuery(id+"F0.imprint","IMPRINT",FACE,{"disambiguationData":[TD([[makeQuery(id+"F0.imprint","IMPRINT",EDGE,{"derivedFrom":sQuery(id+"F0.wireOp",EDGE,"E1")}),1.0]])]});
            extrude(context, id + "F5", {"entities" : qUnion([Q0]), "operationType" : NewBodyOperationType.ADD, "depth" : 12 * mm, "offsetDistance" : 25 * mm, "hasSecondDirection" : true, "secondDirectionOppositeDirection" : false, "secondDirectionDepth" : 1 * mm});
        }
        {
            var Q0;
            Q0=makeQuery(id+"F2.opExtrude","CAP_FACE",FACE,{"disambiguationData":[OSD([sQuery(id+"F0.wireOp",EDGE,"E15"),sQuery(id+"F0.wireOp",EDGE,"E16"),sQuery(id+"F0.wireOp",EDGE,"E17"),sQuery(id+"F0.wireOp",EDGE,"E18"),sQuery(id+"F0.wireOp",EDGE,"E19"),sQuery(id+"F0.wireOp",EDGE,"E20"),sQuery(id+"F0.wireOp",EDGE,"E21"),sQuery(id+"F0.wireOp",EDGE,"E22"),sQuery(id+"F0.wireOp",EDGE,"E23"),sQuery(id+"F0.wireOp",EDGE,"E24")])],"isStart":true});
            fillet(context, id + "F6", {"entities" : qUnion([Q0]), "radius" : 1 * mm, "tangentPropagation" : true, "rho" : .1, "crossSection" : FilletCrossSection.CONIC, "allowEdgeOverflow" : false});
        }
        {
            var Q0;
            {var subQ0=sQuery(id+"F0.wireOp",EDGE,"E3");var subQ1=makeQuery(id+"F0.imprint","INTERSECT",VERTEX,{"derivedFrom":[subQ0,sQuery(id+"F0.wireOp",EDGE,"E11")]});var subQ2=makeQuery(id+"F0.imprint","INTERSECT",VERTEX,{"derivedFrom":[subQ0,sQuery(id+"F0.wireOp",EDGE,"E20")]});var subQ3=makeQuery(id+"F0.imprint","INTERSECT",VERTEX,{"derivedFrom":[subQ0,sQuery(id+"F0.wireOp",EDGE,"E21")]});var subQ4=makeQuery(id+"F0.imprint","INTERSECT",VERTEX,{"derivedFrom":[subQ0,sQuery(id+"F0.wireOp",EDGE,"E12")]});var subQ5=makeQuery(id+"F0.imprint","INTERSECT",VERTEX,{"derivedFrom":[subQ0,sQuery(id+"F0.wireOp",EDGE,"E22")]});var subQ6=makeQuery(id+"F0.imprint","INTERSECT",VERTEX,{"derivedFrom":[subQ0,sQuery(id+"F0.wireOp",EDGE,"E23")]});var subQ7=makeQuery(id+"F0.imprint","INTERSECT",VERTEX,{"derivedFrom":[subQ0,sQuery(id+"F0.wireOp",EDGE,"E13")]});var subQ8=makeQuery(id+"F0.imprint","INTERSECT",VERTEX,{"derivedFrom":[subQ0,sQuery(id+"F0.wireOp",EDGE,"E24")]});var subQ9=makeQuery(id+"F0.imprint","INTERSECT",VERTEX,{"derivedFrom":[subQ0,sQuery(id+"F0.wireOp",EDGE,"E15")]});var subQ10=makeQuery(id+"F0.imprint","INTERSECT",VERTEX,{"derivedFrom":[subQ0,sQuery(id+"F0.wireOp",EDGE,"E14")]});var subQ11=makeQuery(id+"F0.imprint","INTERSECT",VERTEX,{"derivedFrom":[subQ0,sQuery(id+"F0.wireOp",EDGE,"E16")]});var subQ12=makeQuery(id+"F0.imprint","INTERSECT",VERTEX,{"derivedFrom":[subQ0,sQuery(id+"F0.wireOp",EDGE,"E17")]});var subQ13=makeQuery(id+"F0.imprint","INTERSECT",VERTEX,{"derivedFrom":[subQ0,sQuery(id+"F0.wireOp",EDGE,"E10")]});var subQ15=makeQuery(id+"F0.imprint","INTERSECT",VERTEX,{"derivedFrom":[subQ0,sQuery(id+"F0.wireOp",EDGE,"E18")]});Q0=makeQuery(id+"F4.boolean.opBoolean","MERGE",EDGE,{"derivedFrom":[makeQuery(id+"F3.opExtrude","CAP_EDGE",EDGE,{"disambiguationData":[OSD([subQ0]),TDD([makeQuery(id+"F0.imprint","IMPRINT",EDGE,{"disambiguationData":[TD([[subQ15,-1.0]])],"derivedFrom":subQ0})])],"isStart":false}),makeQuery(id+"F3.opExtrude","CAP_EDGE",EDGE,{"disambiguationData":[OSD([subQ0]),TDD([makeQuery(id+"F0.imprint","IMPRINT",EDGE,{"disambiguationData":[TD([[subQ11,-1.0]])],"derivedFrom":subQ0})])],"isStart":false}),makeQuery(id+"F3.opExtrude","CAP_EDGE",EDGE,{"disambiguationData":[OSD([subQ0]),TDD([makeQuery(id+"F0.imprint","IMPRINT",EDGE,{"disambiguationData":[TD([[subQ8,-1.0]])],"derivedFrom":subQ0})])],"isStart":false}),makeQuery(id+"F3.opExtrude","CAP_EDGE",EDGE,{"disambiguationData":[OSD([subQ0]),TDD([makeQuery(id+"F0.imprint","IMPRINT",EDGE,{"disambiguationData":[TD([[subQ5,-1.0]])],"derivedFrom":subQ0})])],"isStart":false}),makeQuery(id+"F3.opExtrude","CAP_EDGE",EDGE,{"disambiguationData":[OSD([subQ0]),TDD([makeQuery(id+"F0.imprint","IMPRINT",EDGE,{"disambiguationData":[TD([[subQ2,-1.0]])],"derivedFrom":subQ0})])],"isStart":false}),makeQuery(id+"F4.opExtrude","CAP_EDGE",EDGE,{"disambiguationData":[OSD([subQ0]),TDD([makeQuery(id+"F0.imprint","IMPRINT",EDGE,{"disambiguationData":[TD([[subQ15,1.0]])],"derivedFrom":subQ0}),makeQuery(id+"F0.imprint","IMPRINT",EDGE,{"disambiguationData":[TD([[subQ13,1.0]])],"derivedFrom":subQ0})])],"isStart":false}),makeQuery(id+"F4.opExtrude","CAP_EDGE",EDGE,{"disambiguationData":[OSD([subQ0]),TDD([makeQuery(id+"F0.imprint","IMPRINT",EDGE,{"disambiguationData":[TD([[subQ12,-1.0]])],"derivedFrom":subQ0}),makeQuery(id+"F0.imprint","IMPRINT",EDGE,{"disambiguationData":[TD([[subQ10,-1.0]])],"derivedFrom":subQ0})])],"isStart":false}),makeQuery(id+"F4.opExtrude","CAP_EDGE",EDGE,{"disambiguationData":[OSD([subQ0]),TDD([makeQuery(id+"F0.imprint","IMPRINT",EDGE,{"disambiguationData":[TD([[subQ9,-1.0]])],"derivedFrom":subQ0}),makeQuery(id+"F0.imprint","IMPRINT",EDGE,{"disambiguationData":[TD([[subQ7,-1.0]])],"derivedFrom":subQ0})])],"isStart":false}),makeQuery(id+"F4.opExtrude","CAP_EDGE",EDGE,{"disambiguationData":[OSD([subQ0]),TDD([makeQuery(id+"F0.imprint","IMPRINT",EDGE,{"disambiguationData":[TD([[subQ6,-1.0]])],"derivedFrom":subQ0}),makeQuery(id+"F0.imprint","IMPRINT",EDGE,{"disambiguationData":[TD([[subQ4,-1.0]])],"derivedFrom":subQ0})])],"isStart":false}),makeQuery(id+"F4.opExtrude","CAP_EDGE",EDGE,{"disambiguationData":[OSD([subQ0]),TDD([makeQuery(id+"F0.imprint","IMPRINT",EDGE,{"disambiguationData":[TD([[subQ3,-1.0]])],"derivedFrom":subQ0}),makeQuery(id+"F0.imprint","IMPRINT",EDGE,{"disambiguationData":[TD([[subQ1,-1.0]])],"derivedFrom":subQ0})])],"isStart":false})]});}
            chamfer(context, id + "F7", {"entities" : qUnion([Q0]), "width" : 0.5 * mm, "tangentPropagation" : true});
        }
        {
            var Q0;
            Q0=makeQuery(id+"F1.opExtrude","CAP_EDGE",EDGE,{"disambiguationData":[OSD([sQuery(id+"F0.wireOp",EDGE,"E2")])],"isStart":false});
            var Q1;
            Q1=makeQuery(id+"F1.opExtrude","CAP_EDGE",EDGE,{"disambiguationData":[OSD([sQuery(id+"F0.wireOp",EDGE,"E2")])],"isStart":true});
            fillet(context, id + "F8", {"entities" : qUnion([Q0, Q1]), "radius" : 1 * mm, "tangentPropagation" : true, "allowEdgeOverflow" : false});
        }
        {
            var Q0;
            Q0=makeQuery(id+"F1.opExtrude","SWEPT_BODY",BODY,{"disambiguationData":[OSD([sQuery(id+"F0.wireOp",EDGE,"E2"),sQuery(id+"F0.wireOp",EDGE,"E3"),sQuery(id+"F0.wireOp",EDGE,"E15"),sQuery(id+"F0.wireOp",EDGE,"E16"),sQuery(id+"F0.wireOp",EDGE,"E17"),sQuery(id+"F0.wireOp",EDGE,"E18"),sQuery(id+"F0.wireOp",EDGE,"E19"),sQuery(id+"F0.wireOp",EDGE,"E20"),sQuery(id+"F0.wireOp",EDGE,"E21"),sQuery(id+"F0.wireOp",EDGE,"E22"),sQuery(id+"F0.wireOp",EDGE,"E23"),sQuery(id+"F0.wireOp",EDGE,"E24")])]});
            transform(context, id + "F9", {"entities" : qUnion([Q0]), "transformType" : TransformType.TRANSLATION_3D, "dx" : 60 * mm, "dy" : 30 * mm, "dz" : 0 * mm, "makeCopy" : false});
        }
    });
